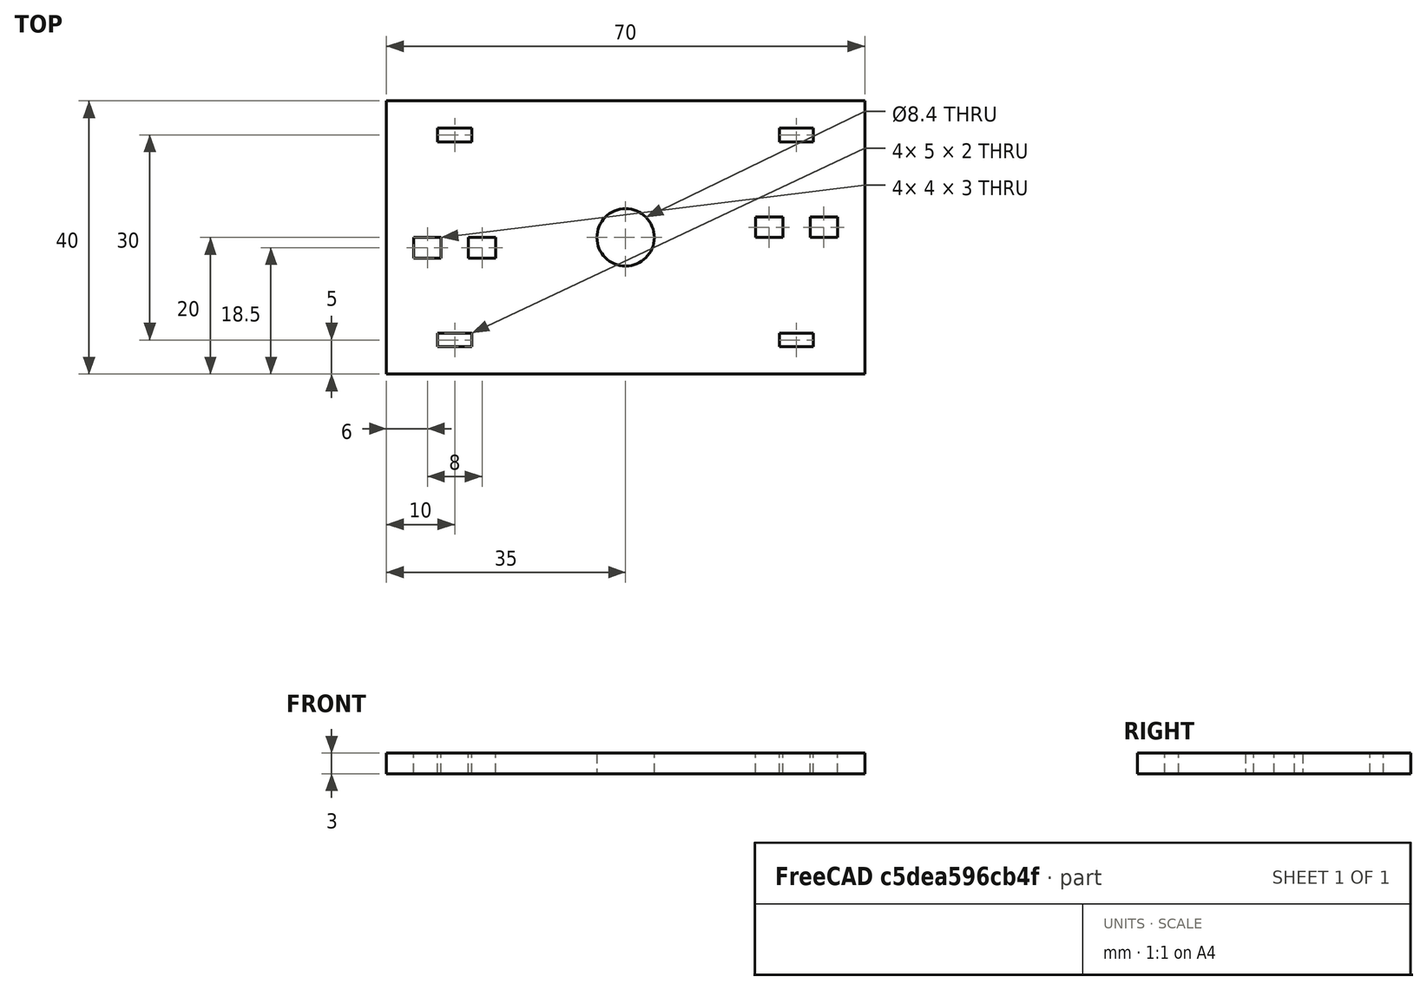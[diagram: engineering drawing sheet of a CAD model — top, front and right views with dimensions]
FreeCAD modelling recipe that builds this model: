
FCSTD DOCUMENT  (FreeCAD 0.17R13519 (Git))
Label: InnerBearingHolder
License: All rights reserved
LicenseURL: http://en.wikipedia.org/wiki/All_rights_reserved
objects: Sketcher::SketchObject×1, PartDesign::Pad×1, PartDesign::Body×1
note: 4 computed .brp shape members not serialized (recipe doc carries the construction recipe); baked Part::Feature solids carry a one-line shape summary decoded from their .brp

FEATURE [Sketcher::SketchObject] Sketch
  MapMode = 5
  Support = -> [XY_Plane]
  sketch-geometry (45):
    g0: LineSegment StartX=-35 StartY=20 StartZ=0 EndX=35 EndY=20 EndZ=0
    g1: LineSegment StartX=35 StartY=20 StartZ=0 EndX=35 EndY=-20 EndZ=0
    g2: LineSegment StartX=35 StartY=-20 StartZ=0 EndX=-35 EndY=-20 EndZ=0
    g3: LineSegment StartX=-35 StartY=-20 StartZ=0 EndX=-35 EndY=20 EndZ=0
    g4: LineSegment [constr] StartX=-25 StartY=20 StartZ=0 EndX=-25 EndY=-20 EndZ=0
    g5: LineSegment [constr] StartX=25 StartY=20 StartZ=0 EndX=25 EndY=-20 EndZ=0
    g6: LineSegment [constr] StartX=-35 StartY=-15 StartZ=0 EndX=35 EndY=-15 EndZ=0
    g7: LineSegment [constr] StartX=35 StartY=15 StartZ=0 EndX=-35 EndY=15 EndZ=0
    g8: LineSegment StartX=-27.5 StartY=16 StartZ=0 EndX=-22.5 EndY=16 EndZ=0
    g9: LineSegment StartX=-22.5 StartY=16 StartZ=0 EndX=-22.5 EndY=14 EndZ=0
    g10: LineSegment StartX=-22.5 StartY=14 StartZ=0 EndX=-27.5 EndY=14 EndZ=0
    g11: LineSegment StartX=-27.5 StartY=14 StartZ=0 EndX=-27.5 EndY=16 EndZ=0
    g12: LineSegment StartX=22.5 StartY=16 StartZ=0 EndX=27.5 EndY=16 EndZ=0
    g13: LineSegment StartX=27.5 StartY=16 StartZ=0 EndX=27.5 EndY=14 EndZ=0
    g14: LineSegment StartX=27.5 StartY=14 StartZ=0 EndX=22.5 EndY=14 EndZ=0
    g15: LineSegment StartX=22.5 StartY=14 StartZ=0 EndX=22.5 EndY=16 EndZ=0
    g16: LineSegment StartX=22.5 StartY=-14 StartZ=0 EndX=27.5 EndY=-14 EndZ=0
    g17: LineSegment StartX=27.5 StartY=-14 StartZ=0 EndX=27.5 EndY=-16 EndZ=0
    g18: LineSegment StartX=27.5 StartY=-16 StartZ=0 EndX=22.5 EndY=-16 EndZ=0
    g19: LineSegment StartX=22.5 StartY=-16 StartZ=0 EndX=22.5 EndY=-14 EndZ=0
    g20: LineSegment StartX=-27.5 StartY=-14 StartZ=0 EndX=-22.5 EndY=-14 EndZ=0
    g21: LineSegment StartX=-22.5 StartY=-14 StartZ=0 EndX=-22.5 EndY=-16 EndZ=0
    g22: LineSegment StartX=-22.5 StartY=-16 StartZ=0 EndX=-27.5 EndY=-16 EndZ=0
    g23: LineSegment StartX=-27.5 StartY=-16 StartZ=0 EndX=-27.5 EndY=-14 EndZ=0
    g24: Circle CenterX=0 CenterY=0 CenterZ=0 NormalX=0 NormalY=0 NormalZ=1 AngleXU=0 Radius=4.2
    g25: LineSegment StartX=-31 StartY=0 StartZ=0 EndX=-27 EndY=0 EndZ=0
    g26: LineSegment StartX=-27 StartY=0 StartZ=0 EndX=-27 EndY=-3 EndZ=0
    g27: LineSegment StartX=-27 StartY=-3 StartZ=0 EndX=-31 EndY=-3 EndZ=0
    g28: LineSegment StartX=-31 StartY=-3 StartZ=0 EndX=-31 EndY=0 EndZ=0
    g29: LineSegment StartX=-23 StartY=0 StartZ=0 EndX=-19 EndY=0 EndZ=0
    g30: LineSegment StartX=-19 StartY=0 StartZ=0 EndX=-19 EndY=-3 EndZ=0
    g31: LineSegment StartX=-19 StartY=-3 StartZ=0 EndX=-23 EndY=-3 EndZ=0
    g32: LineSegment StartX=-23 StartY=-3 StartZ=0 EndX=-23 EndY=0 EndZ=0
    g33: LineSegment [constr] StartX=-27 StartY=-3 StartZ=0 EndX=-23 EndY=-3 EndZ=0
    g34: LineSegment [constr] StartX=-27 StartY=0 StartZ=0 EndX=-23 EndY=0 EndZ=0
    g35: LineSegment StartX=19 StartY=3 StartZ=0 EndX=23 EndY=3 EndZ=0
    g36: LineSegment StartX=23 StartY=3 StartZ=0 EndX=23 EndY=0 EndZ=0
    g37: LineSegment StartX=23 StartY=0 StartZ=0 EndX=19 EndY=0 EndZ=0
    g38: LineSegment StartX=19 StartY=0 StartZ=0 EndX=19 EndY=3 EndZ=0
    g39: LineSegment StartX=27 StartY=3 StartZ=0 EndX=31 EndY=3 EndZ=0
    g40: LineSegment StartX=31 StartY=3 StartZ=0 EndX=31 EndY=0 EndZ=0
    g41: LineSegment StartX=31 StartY=0 StartZ=0 EndX=27 EndY=0 EndZ=0
    g42: LineSegment StartX=27 StartY=0 StartZ=0 EndX=27 EndY=3 EndZ=0
    g43: LineSegment [constr] StartX=27 StartY=3 StartZ=0 EndX=23 EndY=3 EndZ=0
    g44: LineSegment [constr] StartX=23 StartY=0 StartZ=0 EndX=27 EndY=0 EndZ=0
  constraints (128):
    c: Coincident(g0,g1)
    c: Coincident(g1,g2)
    c: Coincident(g2,g3)
    c: Coincident(g3,g0)
    c: Horizontal(g2)
    c: Vertical(g1)
    c: Symmetric(g0,g0,g-2)
    c: Symmetric(g2,g0,g-1)
    c: DistanceX(g0,g0) = 70
    c: DistanceY(g3,g3) = 40
    c: PointOnObject(g4,g0)
    c: PointOnObject(g4,g2)
    c: PointOnObject(g5,g0)
    c: PointOnObject(g5,g2)
    c: PointOnObject(g6,g3)
    c: PointOnObject(g6,g1)
    c: PointOnObject(g7,g3)
    c: Symmetric(g4,g5,g-2)
    c: Symmetric(g7,g6,g-1)
    c: PointOnObject(g7,g1)
    c: DistanceY(g6,g7) = 30
    c: DistanceX(g4,g5) = 50
    c: Coincident(g8,g9)
    c: Coincident(g9,g10)
    c: Coincident(g10,g11)
    c: Coincident(g11,g8)
    c: Horizontal(g8)
    c: Horizontal(g10)
    c: Vertical(g9)
    c: Vertical(g11)
    c: Coincident(g12,g13)
    c: Coincident(g13,g14)
    c: Coincident(g14,g15)
    c: Coincident(g15,g12)
    c: Horizontal(g12)
    c: Horizontal(g14)
    c: Vertical(g13)
    c: Vertical(g15)
    c: Coincident(g16,g17)
    c: Coincident(g17,g18)
    c: Coincident(g18,g19)
    c: Coincident(g19,g16)
    c: Horizontal(g16)
    c: Horizontal(g18)
    c: Vertical(g17)
    c: Vertical(g19)
    c: Coincident(g20,g21)
    c: Coincident(g21,g22)
    c: Coincident(g22,g23)
    c: Coincident(g23,g20)
    c: Horizontal(g20)
    c: Horizontal(g22)
    c: Vertical(g21)
    c: Vertical(g23)
    c: Symmetric(g20,g20,g4)
    c: Symmetric(g20,g22,g6)
    c: Symmetric(g8,g8,g4)
    c: Symmetric(g10,g8,g7)
    c: Symmetric(g12,g12,g5)
    c: Symmetric(g12,g14,g7)
    c: Symmetric(g16,g16,g5)
    c: Symmetric(g18,g16,g6)
    c: DistanceX(g8,g8) = 5
    c: DistanceY(g10,g8) = 2
    c: Equal(g8,g12)
    c: Equal(g12,g16)
    c: Equal(g16,g20)
    c: Equal(g11,g23)
    c: Equal(g23,g19)
    c: Equal(g19,g15)
    c: Coincident(g24,g-1)
    c: Radius(g24) = 4.2
    c: Coincident(g25,g26)
    c: Coincident(g26,g27)
    c: Coincident(g27,g28)
    c: Coincident(g28,g25)
    c: Horizontal(g25)
    c: Horizontal(g27)
    c: Vertical(g26)
    c: Vertical(g28)
    c: Coincident(g29,g30)
    c: Coincident(g30,g31)
    c: Coincident(g31,g32)
    c: Coincident(g32,g29)
    c: Horizontal(g29)
    c: Horizontal(g31)
    c: Vertical(g30)
    c: Vertical(g32)
    c: Coincident(g33,g26)
    c: Coincident(g33,g31)
    c: Horizontal(g33)
    c: Coincident(g34,g25)
    c: Coincident(g34,g29)
    c: Horizontal(g34)
    c: Equal(g29,g34)
    c: Equal(g34,g25)
    c: Symmetric(g25,g29,g4)
    c: DistanceX(g25,g29) = 12
    c: DistanceY(g28,g28) = 3
    c: Coincident(g35,g36)
    c: Coincident(g36,g37)
    c: Coincident(g37,g38)
    c: Coincident(g38,g35)
    c: Horizontal(g35)
    c: Horizontal(g37)
    c: Vertical(g36)
    c: Vertical(g38)
    c: Coincident(g39,g40)
    c: Coincident(g40,g41)
    c: Coincident(g41,g42)
    c: Coincident(g42,g39)
    c: Horizontal(g39)
    c: Horizontal(g41)
    c: Vertical(g40)
    c: Vertical(g42)
    c: Coincident(g43,g39)
    c: Coincident(g43,g35)
    c: Horizontal(g43)
    c: Coincident(g44,g36)
    c: Coincident(g44,g41)
    c: Horizontal(g44)
    c: Equal(g35,g43)
    c: Equal(g43,g39)
    c: Symmetric(g35,g39,g5)
    c: Equal(g35,g25)
    c: Equal(g38,g28)
    c: PointOnObject(g25,g-1)
    c: PointOnObject(g37,g-1)
FEATURE [PartDesign::Pad] Pad
  Length = 3
  Length2 = 100
  Profile = -> Sketch
  Refine = true
  Type = 0
FEATURE [PartDesign::Body] Body
  Group = -> [Sketch,Pad]
  Origin = -> Origin
  Tip = -> Pad
